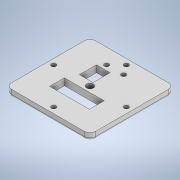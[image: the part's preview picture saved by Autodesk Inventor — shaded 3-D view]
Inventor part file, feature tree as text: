
AUTODESK INVENTOR PART (.ipt)
format: ipt  version: 2020 (Build 240168000, 168)  size: 158,208 bytes
history: native  units: in
note: dims shown in document units (in); Inventor stores cm internally (conversion verified against a paired STEP export)
features: extrude x3, sketch x3, fillet x2, pattern_circular x1
ambient origin geometry x8: Origin, YZ Plane, XZ Plane, XY Plane, X Axis, Y Axis, Z Axis, Center Point
bodies: Solid1 (feature_tree)
feature tree (9):
  extrude  "Extrusion1"  Depth=2.9134in
  fillet  "Fillet1"  Radius=0.2362in
  fillet  "Fillet2"  Radius=0.1969in
  extrude  "Extrusion6"  Depth=0.2362in
  extrude  "Extrusion7"  Depth=0.3937in
  pattern_circular  "Circular Pattern1"  [2 undecoded]
  sketch  "Sketch1"  dims[d0=2.9134in d1=2.9134in d2=0.2362in d3=0.0in d4=0.1969in]
  sketch  "Sketch6"  dims[d24=0.0787in d29=0.2362in]
  sketch  "Sketch7"  dims[d30=0.1575in d31=0.1575in d32=0.4724in d33=0.5906in d34=1.378in d35=0.5118in d36=0.3937in d37=0.0in d38=0.1575in d39=0.3937in d40=0.0in d41=1.5748in d42=360.0deg]
note: 2 required parameter values undecoded (feature->parameter linkage not recoverable at this tier; creation-order binding heuristic only, values carry confidence <= 0.55)
